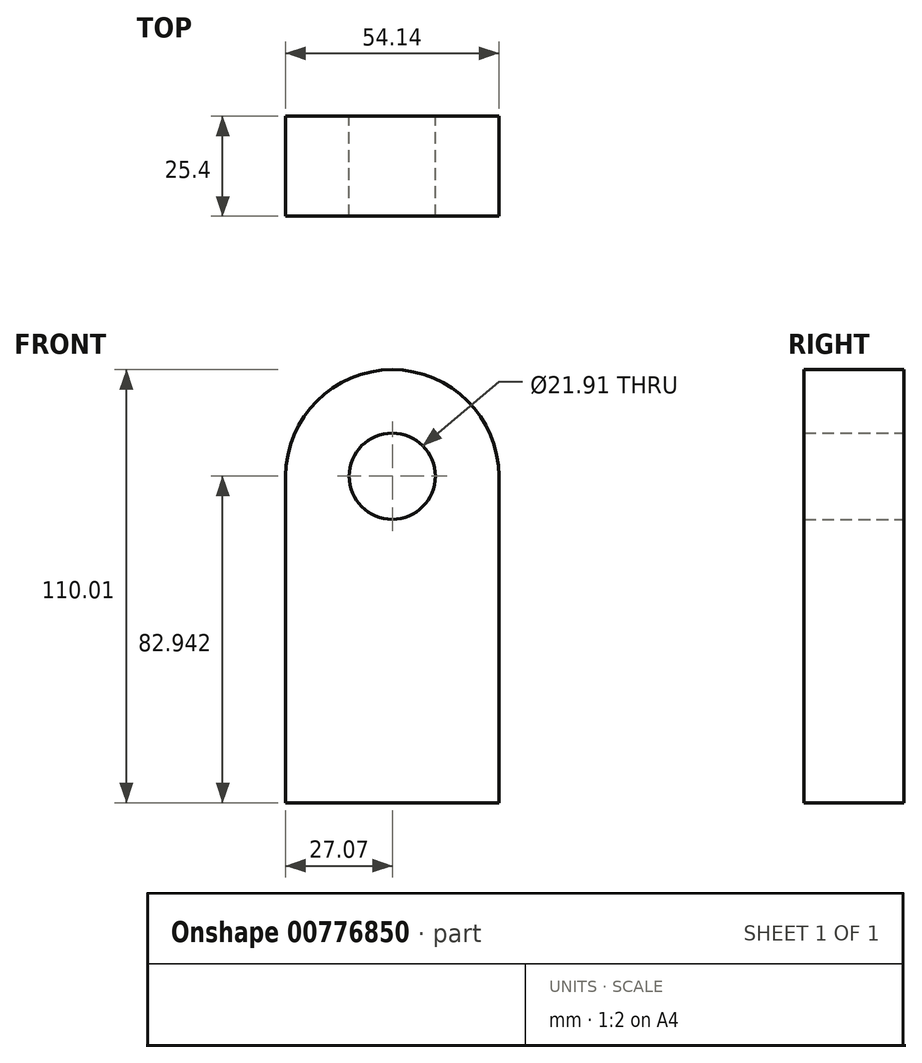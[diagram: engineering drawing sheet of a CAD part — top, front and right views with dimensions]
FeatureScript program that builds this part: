
annotation { "Feature Type Name" : "Feature", "Feature Type Description" : "" }
export const myFeature = defineFeature(function(context is Context, id is Id, definition is map)
    precondition{}
    {
        {
            var Q0;
            Q0=qCreatedBy(makeId("Front.planeOp"),FACE);
            var sketch = newSketch(context, id + "F0", { "sketchPlane" : qUnion([Q0])});
            skLineSegment(sketch, "E0.bottom", {"start": v(-27.07, 41.47) * mm, "end": v(27.07, 41.47) * mm});
            skLineSegment(sketch, "E0.top", {"start": v(-27.07, -41.47) * mm, "end": v(27.07, -41.47) * mm});
            skLineSegment(sketch, "E0.left", {"start": v(-27.07, 41.47) * mm, "end": v(-27.07, -41.47) * mm});
            skLineSegment(sketch, "E0.right", {"start": v(27.07, 41.47) * mm, "end": v(27.07, -41.47) * mm});
            skPoint(sketch, "E0.middle", {"position": v(0, 0) * mm});
            skArc(sketch, "E1", {"start": v(27.07, 41.47) * mm, "mid": v(0, 68.54) * mm, "end": v(-27.07, 41.47) * mm});
            skCircle(sketch, "E2", {"center": v(0, 41.47) * mm, "radius": 10.96 * mm});
            skSolve(sketch);
        }
        {
            var Q0;
            {var subQ0=sQuery(id+"F0.wireOp",EDGE,"E1");Q0=makeQuery(id+"F0.imprint","IMPRINT",FACE,{"disambiguationData":[TD([[makeQuery(id+"F0.imprint","IMPRINT",EDGE,{"derivedFrom":subQ0}),1.0]])]});}
            var Q1;
            Q1=makeQuery(id+"F0.imprint","IMPRINT",FACE,{"disambiguationData":[TD([[makeQuery(id+"F0.imprint","IMPRINT",EDGE,{"derivedFrom":sQuery(id+"F0.wireOp",EDGE,"E0.top")}),1.0]])]});
            extrude(context, id + "F1", {"entities" : qUnion([Q0, Q1]), "depth" : 25.4 * mm, "offsetDistance" : 25.4 * mm});
        }
    });
